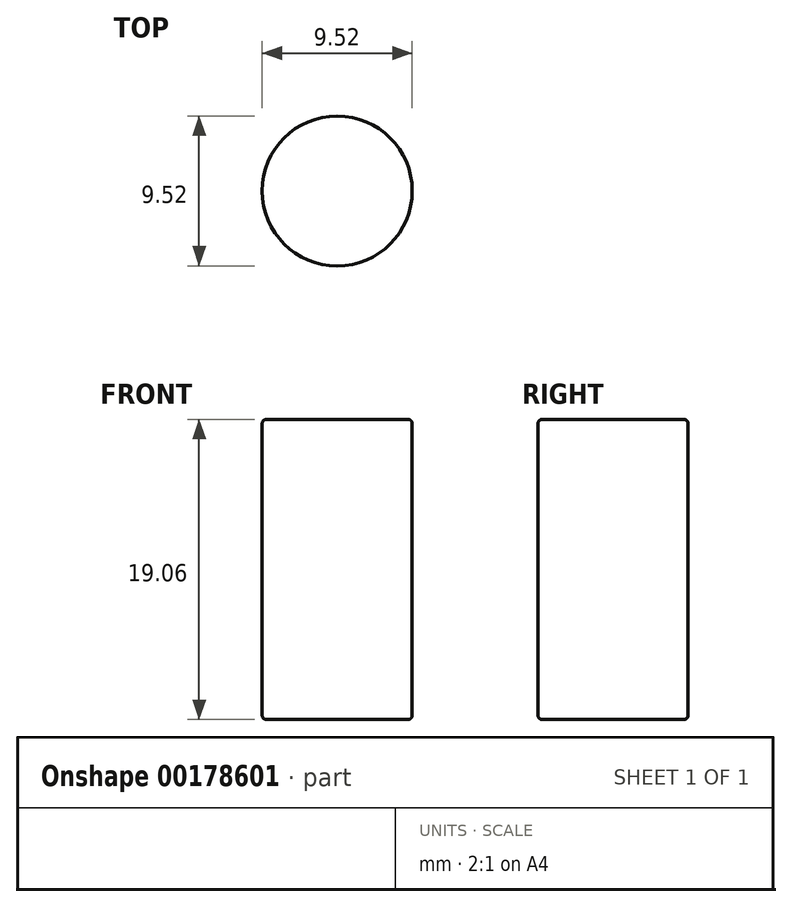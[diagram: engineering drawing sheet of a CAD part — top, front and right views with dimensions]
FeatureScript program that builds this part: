
annotation { "Feature Type Name" : "Feature", "Feature Type Description" : "" }
export const myFeature = defineFeature(function(context is Context, id is Id, definition is map)
    precondition{}
    {
        {
            var Q0;
            Q0=qCreatedBy(makeId("Top.planeOp"),FACE);
            var sketch = newSketch(context, id + "F0", { "sketchPlane" : qUnion([Q0])});
            skCircle(sketch, "E0", {"center": v(0, 0) * mm, "radius": 4.76 * mm});
            skSolve(sketch);
        }
        {
            var Q0;
            Q0 = qSketchRegion(id + "F0", true);
            extrude(context, id + "F1", {"entities" : qUnion([Q0]), "endBound" : BoundingType.SYMMETRIC, "depth" : 19.05 * mm});
        }
        {
            var Q0;
            Q0=makeQuery(id+"F1.opExtrude","CAP_EDGE",EDGE,{"disambiguationData":[OSD([sQuery(id+"F0.wireOp",EDGE,"E0")])],"isStart":false});
            var Q1;
            Q1=makeQuery(id+"F1.opExtrude","CAP_EDGE",EDGE,{"disambiguationData":[OSD([sQuery(id+"F0.wireOp",EDGE,"E0")])],"isStart":true});
            fillet(context, id + "F2", {"entities" : qUnion([Q0, Q1]), "radius" : 0.25 * mm, "tangentPropagation" : true, "allowEdgeOverflow" : false});
        }
    });
